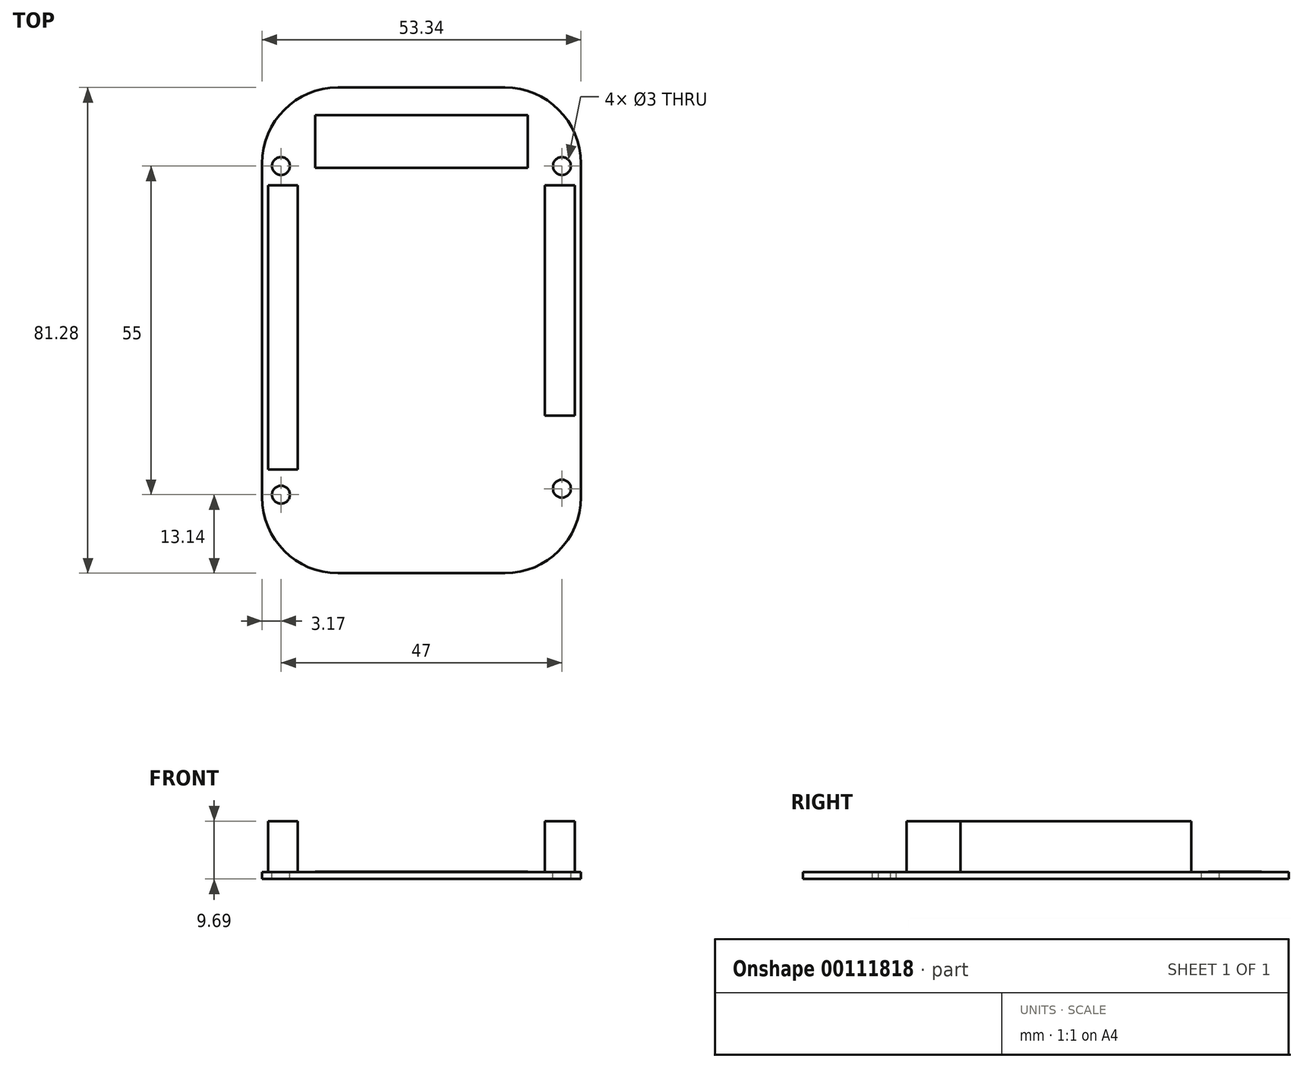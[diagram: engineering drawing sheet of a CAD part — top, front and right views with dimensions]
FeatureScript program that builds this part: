
annotation { "Feature Type Name" : "Feature", "Feature Type Description" : "" }
export const myFeature = defineFeature(function(context is Context, id is Id, definition is map)
    precondition{}
    {
        {
            var Q0;
            Q0=qCreatedBy(makeId("Top.planeOp"),FACE);
            var sketch = newSketch(context, id + "F0", { "sketchPlane" : qUnion([Q0])});
            skLineSegment(sketch, "E0.bottom", {"start": v(13.97, -40.64) * mm, "end": v(-13.97, -40.64) * mm});
            skLineSegment(sketch, "E0.top", {"start": v(13.97, 40.64) * mm, "end": v(-13.97, 40.64) * mm});
            skLineSegment(sketch, "E0.left", {"start": v(26.67, -27.94) * mm, "end": v(26.67, 27.94) * mm});
            skLineSegment(sketch, "E0.right", {"start": v(-26.67, -27.94) * mm, "end": v(-26.67, 27.94) * mm});
            skPoint(sketch, "E0.middle", {"position": v(0, 0) * mm});
            skPoint(sketch, "E1.visualSharp", {"position": v(-26.67, 40.64) * mm});
            skArc(sketch, "E1.filletArc", {"start": v(-13.97, 40.64) * mm, "mid": v(-22.95, 36.92) * mm, "end": v(-26.67, 27.94) * mm});
            skPoint(sketch, "E2.visualSharp", {"position": v(26.67, 40.64) * mm});
            skArc(sketch, "E2.filletArc", {"start": v(26.67, 27.94) * mm, "mid": v(22.95, 36.92) * mm, "end": v(13.97, 40.64) * mm});
            skPoint(sketch, "E3.visualSharp", {"position": v(26.67, -40.64) * mm});
            skArc(sketch, "E3.filletArc", {"start": v(13.97, -40.64) * mm, "mid": v(22.95, -36.92) * mm, "end": v(26.67, -27.94) * mm});
            skPoint(sketch, "E4.visualSharp", {"position": v(-26.67, -40.64) * mm});
            skArc(sketch, "E4.filletArc", {"start": v(-26.67, -27.94) * mm, "mid": v(-22.95, -36.92) * mm, "end": v(-13.97, -40.64) * mm});
            skSolve(sketch);
        }
        {
            var Q0;
            Q0=makeQuery(id+"F0.imprint","IMPRINT",FACE,{"disambiguationData":[TD([[makeQuery(id+"F0.imprint","IMPRINT",EDGE,{"derivedFrom":sQuery(id+"F0.wireOp",EDGE,"E0.bottom")}),-1.0]])]});
            extrude(context, id + "F1", {"entities" : qUnion([Q0]), "depth" : 1.2 * mm});
        }
        {
            var Q0;
            Q0=makeQuery(id+"F1.opExtrude","CAP_FACE",FACE,{"disambiguationData":[OSD([sQuery(id+"F0.wireOp",EDGE,"E0.bottom"),sQuery(id+"F0.wireOp",EDGE,"E0.top"),sQuery(id+"F0.wireOp",EDGE,"E0.left"),sQuery(id+"F0.wireOp",EDGE,"E0.right"),sQuery(id+"F0.wireOp",EDGE,"E1.filletArc"),sQuery(id+"F0.wireOp",EDGE,"E2.filletArc"),sQuery(id+"F0.wireOp",EDGE,"E3.filletArc"),sQuery(id+"F0.wireOp",EDGE,"E4.filletArc")])],"isStart":false});
            var sketch = newSketch(context, id + "F2", { "sketchPlane" : qUnion([Q0])});
            skCircle(sketch, "E5", {"center": v(-23.5, 27.5) * mm, "radius": 1.5 * mm});
            skLineSegment(sketch, "E6", {"start": v(0, 40.64) * mm, "end": v(0, -40.64) * mm, "construction": true});
            skLineSegment(sketch, "E7", {"start": v(26.67, 0) * mm, "end": v(-26.67, 0) * mm, "construction": true});
            skCircle(sketch, "E8.MirrorC", {"center": v(23.5, 27.5) * mm, "radius": 1.5 * mm});
            skCircle(sketch, "E9.MirrorC", {"center": v(-23.5, -27.5) * mm, "radius": 1.5 * mm});
            skCircle(sketch, "E10.MirrorC", {"center": v(23.5, -26.5) * mm, "radius": 1.5 * mm});
            skSolve(sketch);
        }
        {
            var Q0;
            Q0 = qSketchRegion(id + "F2", true);
            extrude(context, id + "F3", {"entities" : qUnion([Q0]), "operationType" : NewBodyOperationType.REMOVE, "endBound" : BoundingType.THROUGH_ALL, "oppositeDirection" : true, "depth" : 25.4 * mm});
        }
        {
            var Q0;
            Q0=makeQuery(id+"F1.opExtrude","CAP_FACE",FACE,{"disambiguationData":[OSD([sQuery(id+"F0.wireOp",EDGE,"E0.bottom"),sQuery(id+"F0.wireOp",EDGE,"E0.top"),sQuery(id+"F0.wireOp",EDGE,"E0.left"),sQuery(id+"F0.wireOp",EDGE,"E0.right"),sQuery(id+"F0.wireOp",EDGE,"E1.filletArc"),sQuery(id+"F0.wireOp",EDGE,"E2.filletArc"),sQuery(id+"F0.wireOp",EDGE,"E3.filletArc"),sQuery(id+"F0.wireOp",EDGE,"E4.filletArc")])],"isStart":false});
            var sketch = newSketch(context, id + "F4", { "sketchPlane" : qUnion([Q0])});
            skLineSegment(sketch, "E11", {"start": v(-40.38, 24.3) * mm, "end": v(47.85, 24.3) * mm, "construction": true});
            skLineSegment(sketch, "E12.bottom", {"start": v(-25.67, 24.3) * mm, "end": v(-20.67, 24.3) * mm});
            skLineSegment(sketch, "E12.top", {"start": v(-25.67, -23.3) * mm, "end": v(-20.67, -23.3) * mm});
            skLineSegment(sketch, "E12.left", {"start": v(-25.67, 24.3) * mm, "end": v(-25.67, -23.3) * mm});
            skLineSegment(sketch, "E12.right", {"start": v(-20.67, 24.3) * mm, "end": v(-20.67, -23.3) * mm});
            skLineSegment(sketch, "E13.bottom", {"start": v(20.67, 24.3) * mm, "end": v(25.67, 24.3) * mm});
            skLineSegment(sketch, "E13.top", {"start": v(20.67, -14.3) * mm, "end": v(25.67, -14.3) * mm});
            skLineSegment(sketch, "E13.left", {"start": v(20.67, 24.3) * mm, "end": v(20.67, -14.3) * mm});
            skLineSegment(sketch, "E13.right", {"start": v(25.67, 24.3) * mm, "end": v(25.67, -14.3) * mm});
            skSolve(sketch);
        }
        {
            var Q0;
            Q0 = qSketchRegion(id + "F4", true);
            extrude(context, id + "F5", {"entities" : qUnion([Q0]), "operationType" : NewBodyOperationType.ADD, "depth" : 8.5 * mm});
        }
        {
            var Q0;
            Q0=makeQuery(id+"F1.opExtrude","CAP_FACE",FACE,{"disambiguationData":[OSD([sQuery(id+"F0.wireOp",EDGE,"E0.bottom"),sQuery(id+"F0.wireOp",EDGE,"E0.top"),sQuery(id+"F0.wireOp",EDGE,"E0.left"),sQuery(id+"F0.wireOp",EDGE,"E0.right"),sQuery(id+"F0.wireOp",EDGE,"E1.filletArc"),sQuery(id+"F0.wireOp",EDGE,"E2.filletArc"),sQuery(id+"F0.wireOp",EDGE,"E3.filletArc"),sQuery(id+"F0.wireOp",EDGE,"E4.filletArc")])],"isStart":false});
            var sketch = newSketch(context, id + "F6", { "sketchPlane" : qUnion([Q0])});
            skLineSegment(sketch, "E14.bottom", {"start": v(-17.8, 36.04) * mm, "end": v(17.8, 36.04) * mm});
            skLineSegment(sketch, "E14.top", {"start": v(-17.8, 27.2) * mm, "end": v(17.8, 27.2) * mm});
            skLineSegment(sketch, "E14.left", {"start": v(-17.8, 36.04) * mm, "end": v(-17.8, 27.2) * mm});
            skLineSegment(sketch, "E14.right", {"start": v(17.8, 36.04) * mm, "end": v(17.8, 27.2) * mm});
            skSolve(sketch);
        }
        {
            var Q0;
            Q0 = qSketchRegion(id + "F6", true);
            extrude(context, id + "F7", {"entities" : qUnion([Q0]), "operationType" : NewBodyOperationType.ADD, "depth" : 0.03 * mm});
        }
    });
